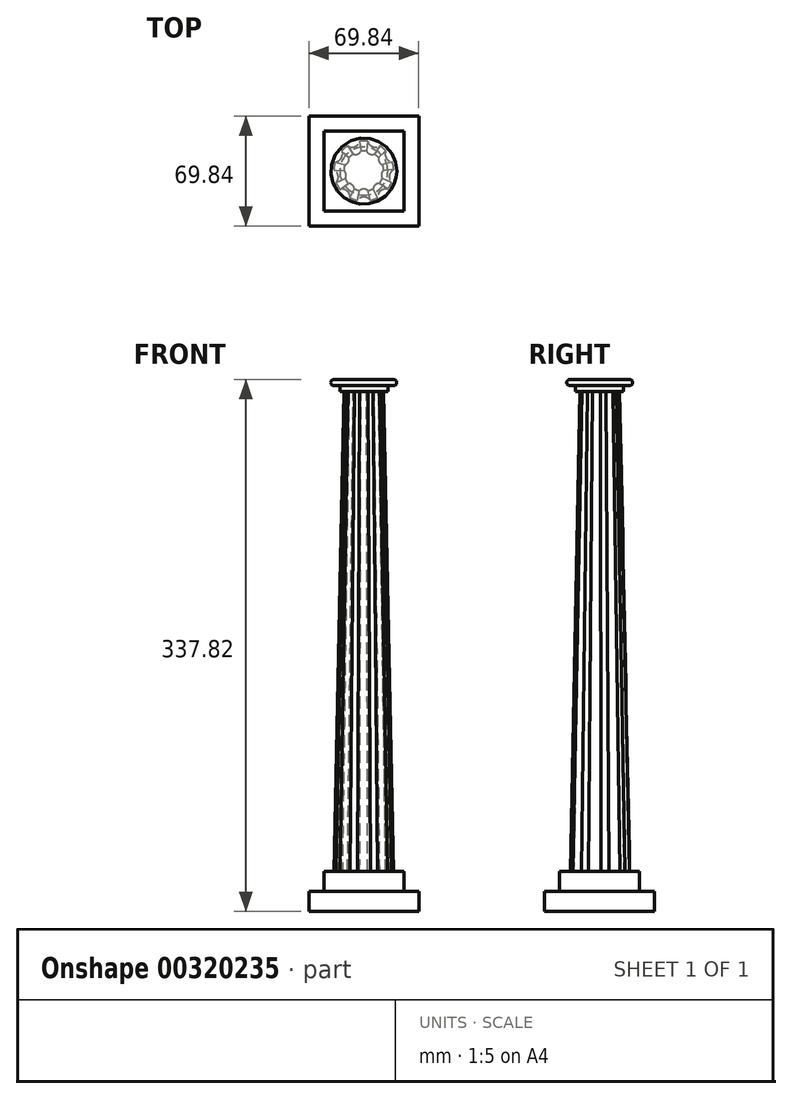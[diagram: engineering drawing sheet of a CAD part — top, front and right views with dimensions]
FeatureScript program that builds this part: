
annotation { "Feature Type Name" : "Feature", "Feature Type Description" : "" }
export const myFeature = defineFeature(function(context is Context, id is Id, definition is map)
    precondition{}
    {
        {
            var Q0;
            Q0=qCreatedBy(makeId("Top.planeOp"),FACE);
            var sketch = newSketch(context, id + "F0", { "sketchPlane" : qUnion([Q0])});
            skLineSegment(sketch, "E0.bottom", {"start": v(-25.4, 25.4) * mm, "end": v(25.4, 25.4) * mm});
            skLineSegment(sketch, "E0.top", {"start": v(-25.4, -25.4) * mm, "end": v(25.4, -25.4) * mm});
            skLineSegment(sketch, "E0.left", {"start": v(-25.4, 25.4) * mm, "end": v(-25.4, -25.4) * mm});
            skLineSegment(sketch, "E0.right", {"start": v(25.4, 25.4) * mm, "end": v(25.4, -25.4) * mm});
            skLineSegment(sketch, "E1.bottom", {"start": v(34.93, 34.93) * mm, "end": v(-34.92, 34.93) * mm});
            skLineSegment(sketch, "E1.top", {"start": v(34.92, -34.93) * mm, "end": v(-34.93, -34.92) * mm});
            skLineSegment(sketch, "E1.left", {"start": v(34.93, 34.92) * mm, "end": v(34.92, -34.93) * mm});
            skLineSegment(sketch, "E1.right", {"start": v(-34.92, 34.93) * mm, "end": v(-34.93, -34.92) * mm});
            skPoint(sketch, "E1.middle", {"position": v(0, 0) * mm});
            skSolve(sketch);
        }
        {
            var Q0;
            Q0=makeQuery(id+"F0.imprint","IMPRINT",FACE,{"disambiguationData":[TD([[makeQuery(id+"F0.imprint","IMPRINT",EDGE,{"derivedFrom":sQuery(id+"F0.wireOp",EDGE,"E0.bottom")}),1.0]])]});
            var Q1;
            Q1=makeQuery(id+"F0.imprint","IMPRINT",FACE,{"disambiguationData":[TD([[makeQuery(id+"F0.imprint","IMPRINT",EDGE,{"derivedFrom":sQuery(id+"F0.wireOp",EDGE,"E0.bottom")}),-1.0]])]});
            extrude(context, id + "F1", {"entities" : qUnion([Q0, Q1]), "depth" : 12.7 * mm});
        }
        {
            var Q0;
            Q0=makeQuery(id+"F0.imprint","IMPRINT",FACE,{"disambiguationData":[TD([[makeQuery(id+"F0.imprint","IMPRINT",EDGE,{"derivedFrom":sQuery(id+"F0.wireOp",EDGE,"E0.bottom")}),-1.0]])]});
            extrude(context, id + "F2", {"entities" : qUnion([Q0]), "operationType" : NewBodyOperationType.ADD, "depth" : 25.4 * mm});
        }
        {
            var Q0;
            Q0=makeQuery(id+"F2.opExtrude","CAP_FACE",FACE,{"disambiguationData":[OSD([sQuery(id+"F0.wireOp",EDGE,"E0.bottom"),sQuery(id+"F0.wireOp",EDGE,"E0.top"),sQuery(id+"F0.wireOp",EDGE,"E0.left"),sQuery(id+"F0.wireOp",EDGE,"E0.right")])],"isStart":false});
            cPlane(context, id + "F3", {"entities" : qUnion([Q0]), "cplaneType" : CPlaneType.OFFSET, "offset" : 304.8 * mm, "width" : 152.4 * mm, "height" : 152.4 * mm});
        }
        {
            var Q0;
            Q0=makeQuery(id+"F2.opExtrude","CAP_FACE",FACE,{"disambiguationData":[OSD([sQuery(id+"F0.wireOp",EDGE,"E0.bottom"),sQuery(id+"F0.wireOp",EDGE,"E0.top"),sQuery(id+"F0.wireOp",EDGE,"E0.left"),sQuery(id+"F0.wireOp",EDGE,"E0.right")])],"isStart":false});
            var sketch = newSketch(context, id + "F4", { "sketchPlane" : qUnion([Q0])});
            skCircle(sketch, "E2", {"center": v(0, 0) * mm, "radius": 19.05 * mm});
            skArc(sketch, "E3", {"start": v(4.16, -18.6) * mm, "mid": v(0.04, -16.5) * mm, "end": v(-4.06, -18.61) * mm});
            skArc(sketch, "E4.1.0", {"start": v(15.14, -11.57) * mm, "mid": v(10.65, -12.62) * mm, "end": v(8.86, -16.87) * mm});
            skArc(sketch, "E4.2.0", {"start": v(19.03, 0.87) * mm, "mid": v(16.27, -2.82) * mm, "end": v(17.63, -7.23) * mm});
            skArc(sketch, "E5.3.3.0", {"start": v(14.02, 12.9) * mm, "mid": v(14.28, 8.3) * mm, "end": v(18.15, 5.8) * mm});
            skArc(sketch, "E5.3.4.0", {"start": v(2.45, 18.9) * mm, "mid": v(5.6, 15.53) * mm, "end": v(10.18, 16.1) * mm});
            skArc(sketch, "E5.3.5.0", {"start": v(-10.27, 16.05) * mm, "mid": v(-5.69, 15.5) * mm, "end": v(-2.55, 18.88) * mm});
            skArc(sketch, "E5.3.6.0", {"start": v(-18.18, 5.7) * mm, "mid": v(-14.32, 8.22) * mm, "end": v(-14.1, 12.82) * mm});
            skArc(sketch, "E5.3.7.0", {"start": v(-17.59, -7.32) * mm, "mid": v(-16.25, -2.91) * mm, "end": v(-19.03, 0.76) * mm});
            skArc(sketch, "E5.3.8.0", {"start": v(-8.76, -16.91) * mm, "mid": v(-10.58, -12.68) * mm, "end": v(-15.07, -11.65) * mm});
            skSolve(sketch);
        }
        {
            var Q0;
            Q0=qCreatedBy(id+"F3.planeOp",FACE);
            var sketch = newSketch(context, id + "F5", { "sketchPlane" : qUnion([Q0])});
            skCircle(sketch, "E6", {"center": v(0, 0) * mm, "radius": 12.7 * mm});
            skArc(sketch, "E7", {"start": v(2.58, -12.44) * mm, "mid": v(0, -11.43) * mm, "end": v(-2.58, -12.44) * mm});
            skArc(sketch, "E8.1.0", {"start": v(9.97, -7.87) * mm, "mid": v(7.35, -8.76) * mm, "end": v(6.02, -11.18) * mm});
            skArc(sketch, "E8.2.0", {"start": v(12.7, 0.38) * mm, "mid": v(11.26, -1.98) * mm, "end": v(11.8, -4.7) * mm});
            skArc(sketch, "E8.3.0", {"start": v(9.48, 8.45) * mm, "mid": v(9.9, 5.72) * mm, "end": v(12.06, 3.98) * mm});
            skArc(sketch, "E8.4.0", {"start": v(1.83, 12.57) * mm, "mid": v(3.9, 10.74) * mm, "end": v(6.68, 10.8) * mm});
            skArc(sketch, "E8.5.0", {"start": v(-6.68, 10.8) * mm, "mid": v(-3.9, 10.74) * mm, "end": v(-1.83, 12.57) * mm});
            skArc(sketch, "E8.6.0", {"start": v(-12.06, 3.98) * mm, "mid": v(-9.9, 5.72) * mm, "end": v(-9.48, 8.45) * mm});
            skArc(sketch, "E8.7.0", {"start": v(-11.8, -4.7) * mm, "mid": v(-11.26, -1.98) * mm, "end": v(-12.7, 0.38) * mm});
            skArc(sketch, "E8.8.0", {"start": v(-6.02, -11.18) * mm, "mid": v(-7.35, -8.76) * mm, "end": v(-9.97, -7.87) * mm});
            skSolve(sketch);
        }
        {
            var Q1;
            {var subQ0=sQuery(id+"F4.wireOp",EDGE,"E3");Q1=makeQuery(id+"F4.imprint","IMPRINT",FACE,{"disambiguationData":[TD([[makeQuery(id+"F4.imprint","IMPRINT",EDGE,{"derivedFrom":subQ0}),-1.0]])]});}
            var Q2;
            {var subQ0=sQuery(id+"F5.wireOp",EDGE,"E7");Q2=makeQuery(id+"F5.imprint","IMPRINT",FACE,{"disambiguationData":[TD([[makeQuery(id+"F5.imprint","IMPRINT",EDGE,{"derivedFrom":subQ0}),-1.0]])]});}
            loft(context, id + "F6", {"operationType" : NewBodyOperationType.ADD, "sheetProfilesArray" : [{ "sheetProfileEntities" : qUnion([Q1]) }, { "sheetProfileEntities" : qUnion([Q2]) }]});
        }
        {
            var Q0;
            Q0=qCreatedBy(makeId("Front.planeOp"),FACE);
            var sketch = newSketch(context, id + "F7", { "sketchPlane" : qUnion([Q0])});
            skLineSegment(sketch, "E9", {"start": v(0, 330.2) * mm, "end": v(15.24, 330.2) * mm});
            skLineSegment(sketch, "E10", {"start": v(15.24, 330.2) * mm, "end": v(15.24, 334) * mm});
            skLineSegment(sketch, "E11", {"start": v(15.24, 334) * mm, "end": v(19.05, 334) * mm});
            skArc(sketch, "E12", {"start": v(19.05, 334) * mm, "mid": v(20.95, 335.91) * mm, "end": v(19.05, 337.82) * mm});
            skLineSegment(sketch, "E13", {"start": v(19.05, 337.82) * mm, "end": v(0, 337.82) * mm});
            skLineSegment(sketch, "E14", {"start": v(0, 337.82) * mm, "end": v(0, 330.2) * mm});
            skSolve(sketch);
        }
        {
            var Q0;
            Q0=makeQuery(id+"F7.imprint","IMPRINT",FACE,{"disambiguationData":[TD([[makeQuery(id+"F7.imprint","IMPRINT",EDGE,{"derivedFrom":sQuery(id+"F7.wireOp",EDGE,"E9")}),1.0]])]});
            var Q1;
            Q1=sQuery(id+"F7.wireOp",EDGE,"E14");
            revolve(context, id + "F8", {"operationType" : NewBodyOperationType.ADD, "entities" : qUnion([Q0]), "axis" : qUnion([Q1]), "revolveType" : RevolveType.FULL});
        }
    });
